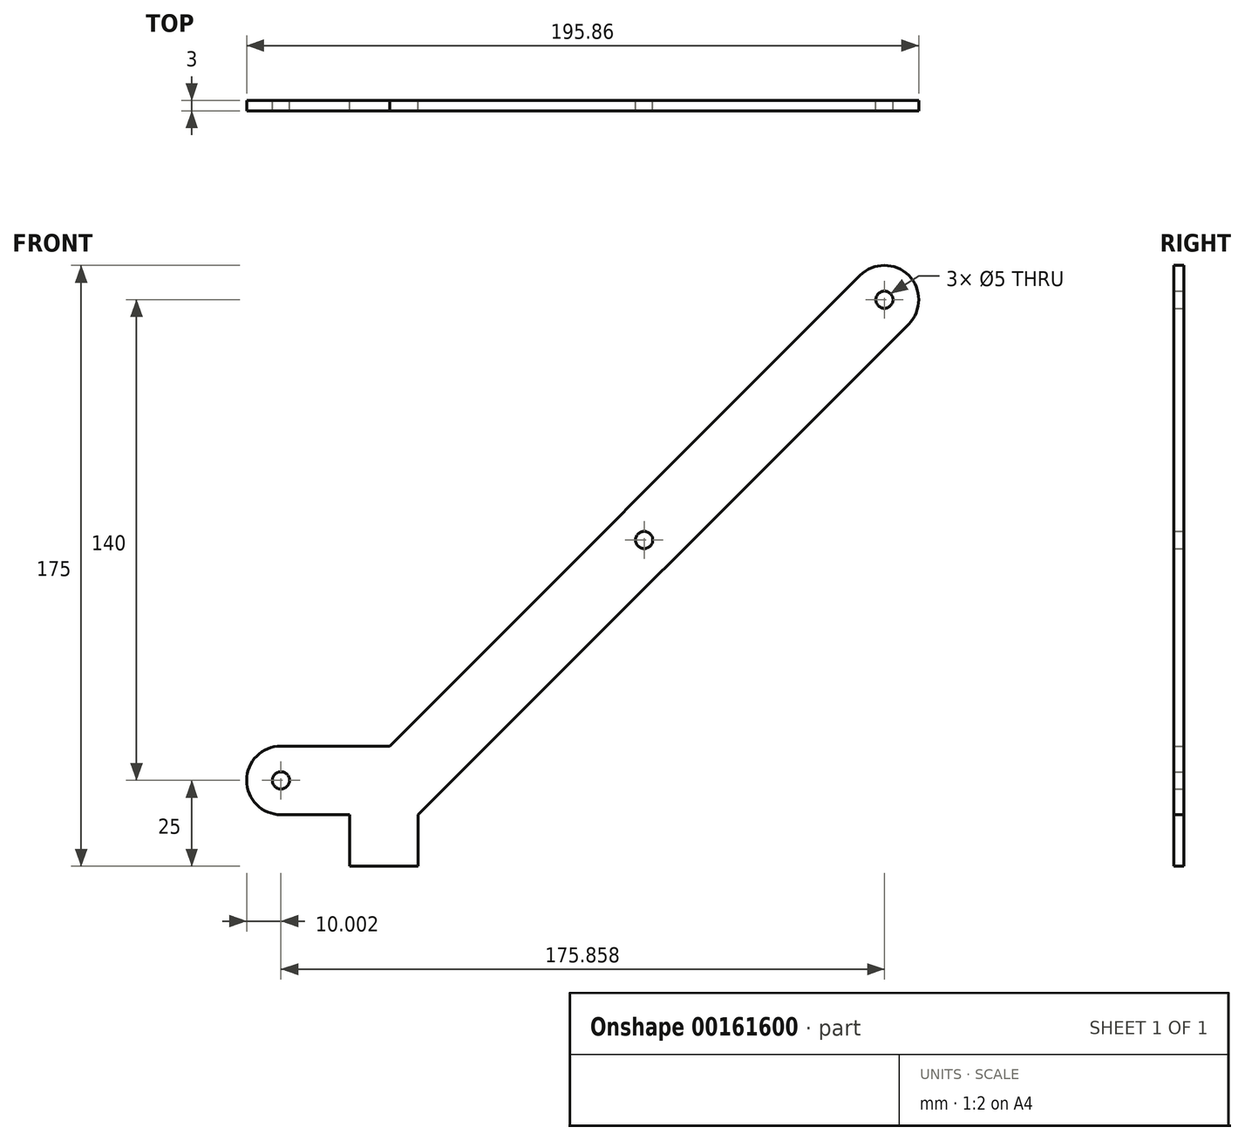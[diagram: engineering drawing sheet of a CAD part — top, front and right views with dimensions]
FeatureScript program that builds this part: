
annotation { "Feature Type Name" : "Feature", "Feature Type Description" : "" }
export const myFeature = defineFeature(function(context is Context, id is Id, definition is map)
    precondition{}
    {
        {
            var Q0;
            Q0=qCreatedBy(makeId("Front.planeOp"),FACE);
            var sketch = newSketch(context, id + "F0", { "sketchPlane" : qUnion([Q0])});
            skLineSegment(sketch, "E0", {"start": v(-35.86, -10) * mm, "end": v(-35.86, 10) * mm, "construction": true});
            skLineSegment(sketch, "E1", {"start": v(-35.86, 10) * mm, "end": v(-4.14, 10) * mm});
            skLineSegment(sketch, "E2", {"start": v(-4.14, 10) * mm, "end": v(132.93, 147.07) * mm});
            skLineSegment(sketch, "E3", {"start": v(132.93, 147.07) * mm, "end": v(147.07, 132.93) * mm, "construction": true});
            skLineSegment(sketch, "E4", {"start": v(147.07, 132.93) * mm, "end": v(4.14, -10) * mm});
            skPoint(sketch, "E5", {"position": v(-35.86, 0) * mm});
            skArc(sketch, "E6", {"start": v(-35.86, 10) * mm, "mid": v(-45.86, 0) * mm, "end": v(-35.86, -10) * mm});
            skArc(sketch, "E7", {"start": v(132.93, 147.07) * mm, "mid": v(147.07, 147.07) * mm, "end": v(147.07, 132.93) * mm});
            skLineSegment(sketch, "E8", {"start": v(-4.14, 10) * mm, "end": v(4.14, -10) * mm, "construction": true});
            skPoint(sketch, "E9", {"position": v(0, 0) * mm});
            skLineSegment(sketch, "E10", {"start": v(140, 140) * mm, "end": v(0, 0) * mm, "construction": true});
            skCircle(sketch, "E11", {"center": v(70, 70) * mm, "radius": 2.5 * mm});
            skCircle(sketch, "E12", {"center": v(-35.86, 0) * mm, "radius": 2.5 * mm});
            skCircle(sketch, "E13", {"center": v(140, 140) * mm, "radius": 2.5 * mm});
            skLineSegment(sketch, "E14", {"start": v(-35.86, -10) * mm, "end": v(-15.86, -10) * mm});
            skLineSegment(sketch, "E15", {"start": v(-15.86, -10) * mm, "end": v(-15.86, -25) * mm});
            skLineSegment(sketch, "E16", {"start": v(-15.86, -25) * mm, "end": v(4.14, -25) * mm});
            skLineSegment(sketch, "E17", {"start": v(4.14, -25) * mm, "end": v(4.14, -10) * mm});
            skSolve(sketch);
        }
        {
            var Q0;
            Q0 = qSketchRegion(id + "F0", true);
            extrude(context, id + "F1", {"entities" : qUnion([Q0]), "endBound" : BoundingType.SYMMETRIC, "depth" : 3 * mm});
        }
    });
